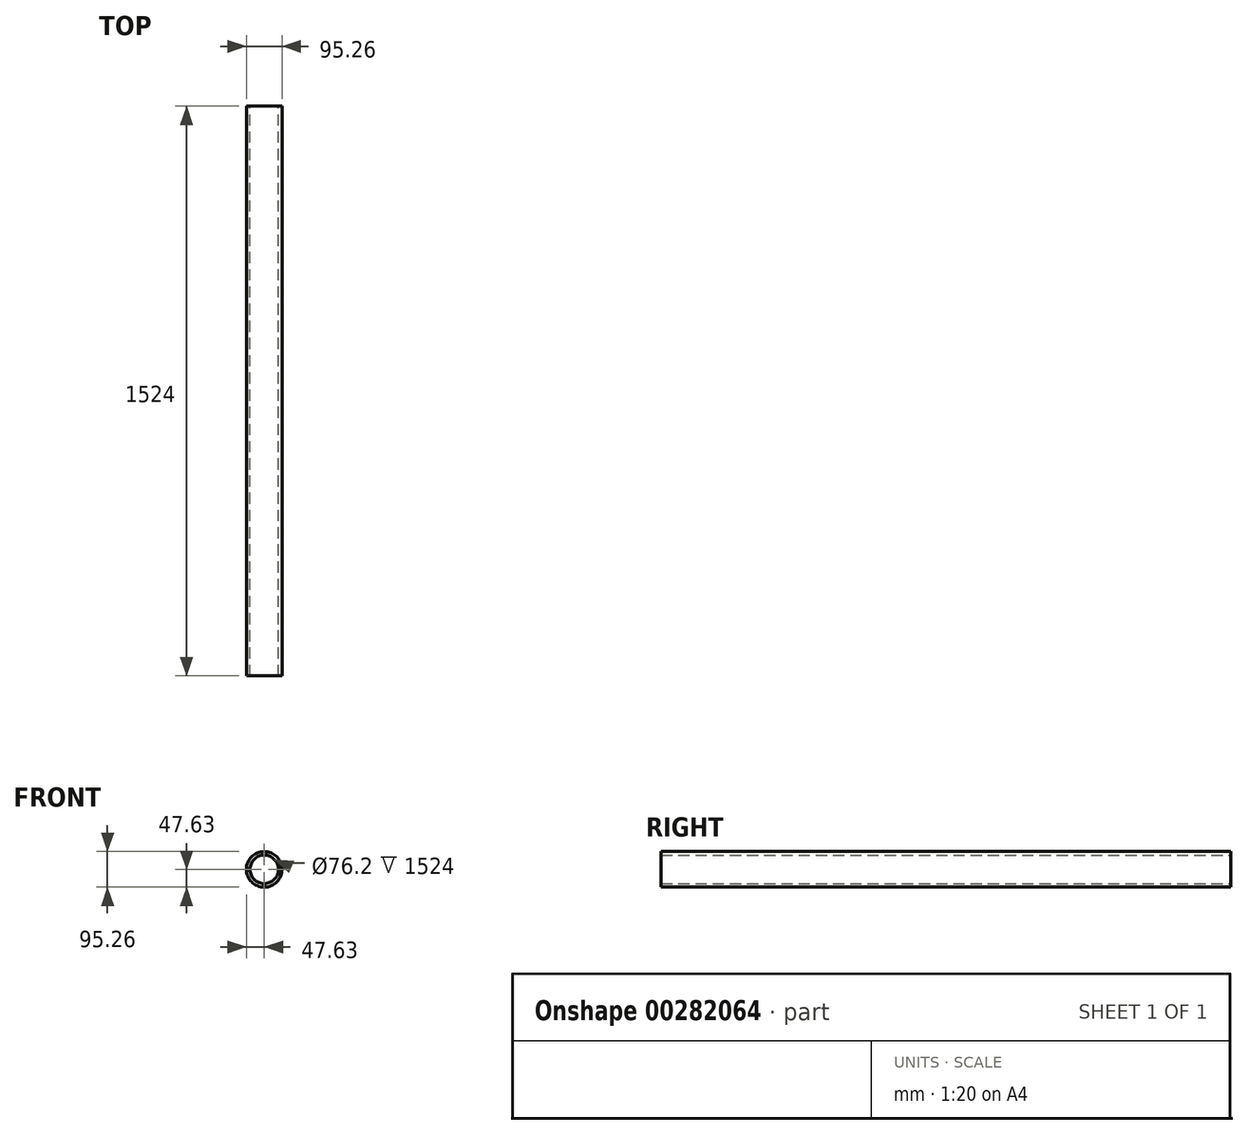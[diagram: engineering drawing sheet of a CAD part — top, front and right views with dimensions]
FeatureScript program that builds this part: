
annotation { "Feature Type Name" : "Feature", "Feature Type Description" : "" }
export const myFeature = defineFeature(function(context is Context, id is Id, definition is map)
    precondition{}
    {
        {
            var Q0;
            Q0=qCreatedBy(makeId("Front.planeOp"),FACE);
            var sketch = newSketch(context, id + "F0", { "sketchPlane" : qUnion([Q0])});
            skCircle(sketch, "E0", {"center": v(0, 0) * mm, "radius": 47.63 * mm});
            skCircle(sketch, "E1", {"center": v(0, 0) * mm, "radius": 38.1 * mm});
            skSolve(sketch);
        }
        {
            var Q0;
            Q0 = qSketchRegion(id + "F0", true);
            extrude(context, id + "F1", {"entities" : qUnion([Q0]), "depth" : 1524 * mm, "offsetDistance" : 25.4 * mm});
        }
    });
